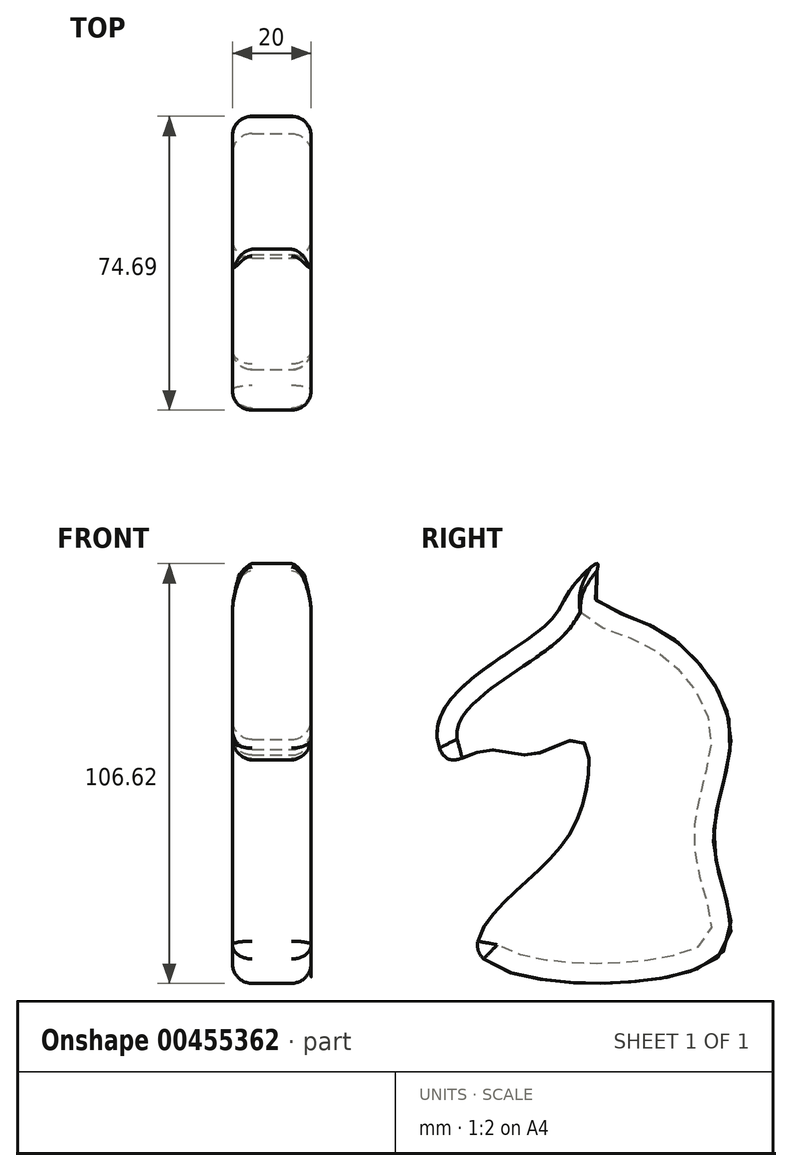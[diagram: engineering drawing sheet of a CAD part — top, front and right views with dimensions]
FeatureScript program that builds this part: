
annotation { "Feature Type Name" : "Feature", "Feature Type Description" : "" }
export const myFeature = defineFeature(function(context is Context, id is Id, definition is map)
    precondition{}
    {
        {
            var Q0;
            Q0=qCreatedBy(makeId("Right.planeOp"),FACE);
            var sketch = newSketch(context, id + "F0", { "sketchPlane" : qUnion([Q0])});
            skFitSpline(sketch, "E0", {"points": [v(-10.92, 35.72) * mm, v(-4.43, 41.63) * mm, v(-5.6, 33.95) * mm, v(9.74, 25.69) * mm, v(29.23, 0) * mm, v(25.1, -30.4) * mm, v(26.28, -58.16) * mm, v(-33.95, -58.16) * mm, v(-21.55, -38.09) * mm, v(-8.56, -20.37) * mm, v(-8.56, -3.25) * mm, v(-20.96, -6.8) * mm, v(-32.77, -5.6) * mm, v(-42.22, -7.97) * mm, v(-44, 3.84) * mm, v(-17.42, 26.28) * mm, v(-10.92, 35.72) * mm]});
            skSolve(sketch);
        }
        {
            var Q0;
            Q0 = qSketchRegion(id + "F0", true);
            extrude(context, id + "F1", {"entities" : qUnion([Q0]), "depth" : 20 * mm});
        }
        {
            var Q0;
            Q0=makeQuery(id+"F1.opExtrude","CAP_EDGE",EDGE,{"disambiguationData":[OSD([sQuery(id+"F0.wireOp",EDGE,"E0")])],"isStart":false});
            var Q1;
            Q1=makeQuery(id+"F1.opExtrude","CAP_EDGE",EDGE,{"disambiguationData":[OSD([sQuery(id+"F0.wireOp",EDGE,"E0")])],"isStart":true});
            fillet(context, id + "F2", {"entities" : qUnion([Q0, Q1]), "radius" : 5 * mm, "tangentPropagation" : true, "allowEdgeOverflow" : false});
        }
    });
